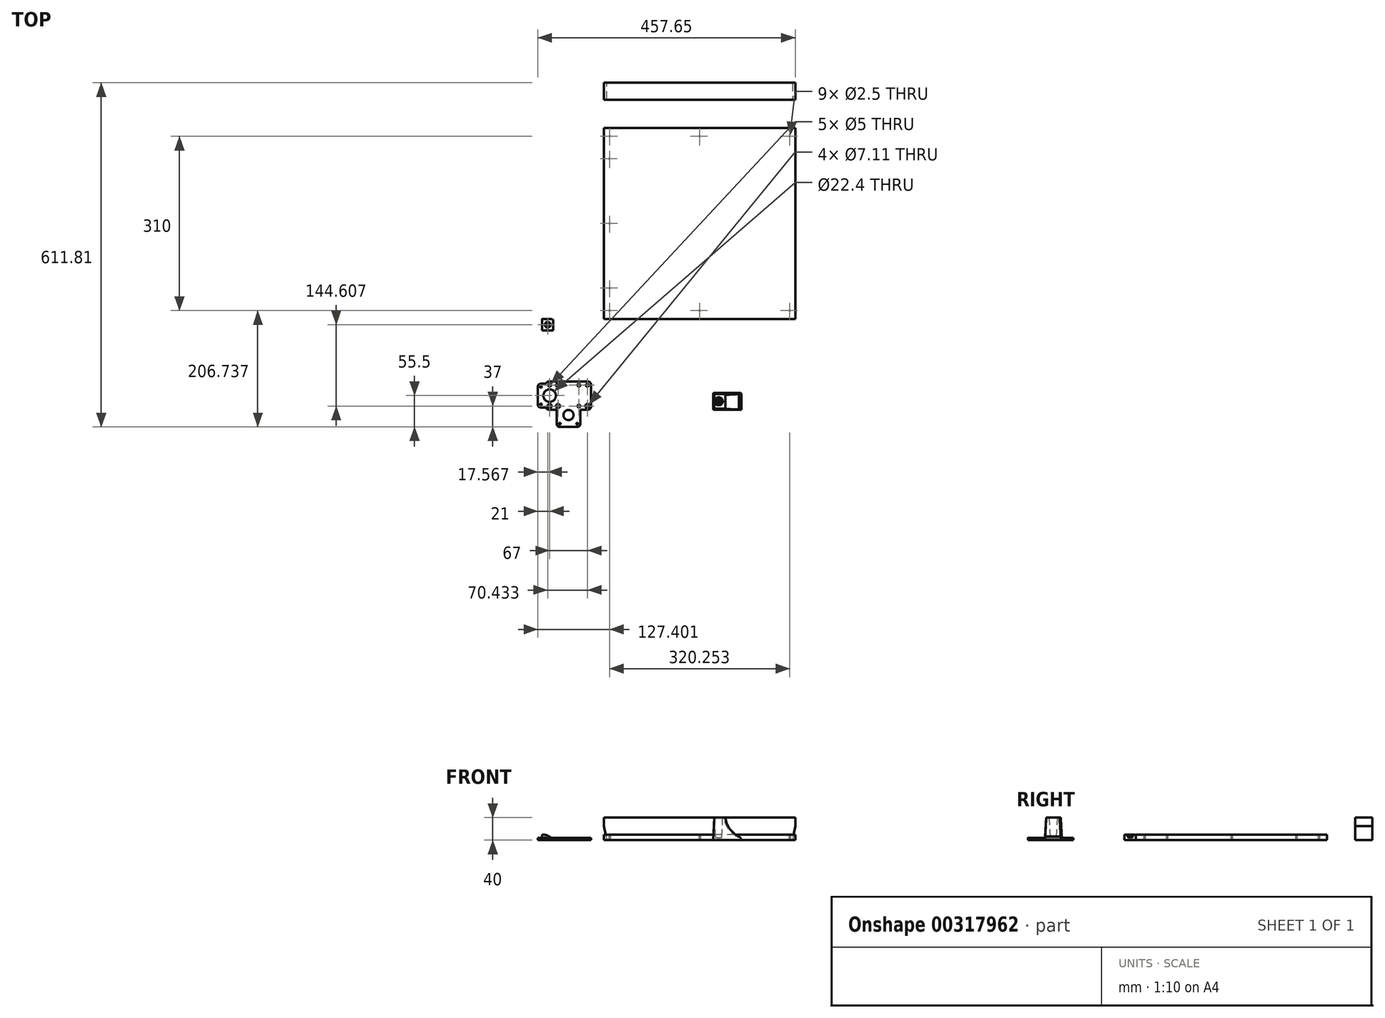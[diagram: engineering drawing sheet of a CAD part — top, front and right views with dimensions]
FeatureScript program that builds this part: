
annotation { "Feature Type Name" : "Feature", "Feature Type Description" : "" }
export const myFeature = defineFeature(function(context is Context, id is Id, definition is map)
    precondition{}
    {
        {
            var Q0;
            Q0=qCreatedBy(makeId("Top.planeOp"),FACE);
            var sketch = newSketch(context, id + "F0", { "sketchPlane" : qUnion([Q0])});
            skLineSegment(sketch, "E0.left", {"start": v(-18.5, 18.5) * mm, "end": v(-18.5, -18.5) * mm, "construction": true});
            skLineSegment(sketch, "E0.right", {"start": v(18.5, 18.5) * mm, "end": v(18.5, -18.5) * mm, "construction": true});
            skCircle(sketch, "E1", {"center": v(-18.5, 18.5) * mm, "radius": 3.56 * mm});
            skCircle(sketch, "E2", {"center": v(18.5, 18.5) * mm, "radius": 2.5 * mm});
            skCircle(sketch, "E3", {"center": v(18.5, -18.5) * mm, "radius": 2.5 * mm});
            skCircle(sketch, "E4", {"center": v(-18.5, -18.5) * mm, "radius": 3.56 * mm});
            skLineSegment(sketch, "E5.bottom", {"start": v(-35, 25) * mm, "end": v(35, 25) * mm});
            skLineSegment(sketch, "E5.top", {"start": v(-35, -25) * mm, "end": v(0.1, -25) * mm});
            skLineSegment(sketch, "E5.right", {"start": v(40, 20) * mm, "end": v(40, -20) * mm});
            skPoint(sketch, "E6.visualSharp", {"position": v(-40, 25) * mm});
            skArc(sketch, "E6.filletArc", {"start": v(-35, 25) * mm, "mid": v(-38.54, 23.54) * mm, "end": v(-40, 20) * mm});
            skPoint(sketch, "E7.visualSharp", {"position": v(40, 25) * mm});
            skArc(sketch, "E7.filletArc", {"start": v(40, 20) * mm, "mid": v(38.54, 23.54) * mm, "end": v(35, 25) * mm});
            skPoint(sketch, "E8.visualSharp", {"position": v(40, -25) * mm});
            skArc(sketch, "E8.filletArc", {"start": v(35, -25) * mm, "mid": v(38.54, -23.54) * mm, "end": v(40, -20) * mm});
            skPoint(sketch, "E9.visualSharp", {"position": v(-40, -25) * mm});
            skArc(sketch, "E9.filletArc", {"start": v(-40, -20) * mm, "mid": v(-38.54, -23.54) * mm, "end": v(-35, -25) * mm});
            skLineSegment(sketch, "E10.bottom", {"start": v(403.15, 136.24) * mm, "end": v(63.15, 136.24) * mm});
            skLineSegment(sketch, "E10.top", {"start": v(403.15, 476.24) * mm, "end": v(63.15, 476.24) * mm});
            skLineSegment(sketch, "E10.left", {"start": v(403.15, 136.24) * mm, "end": v(403.15, 476.24) * mm});
            skLineSegment(sketch, "E10.right", {"start": v(63.15, 136.24) * mm, "end": v(63.15, 476.24) * mm});
            skCircle(sketch, "E11", {"center": v(-33.5, -18.5) * mm, "radius": 3.56 * mm});
            skCircle(sketch, "E12", {"center": v(33.5, -18.5) * mm, "radius": 3.56 * mm});
            skCircle(sketch, "E13", {"center": v(-33.5, 18.5) * mm, "radius": 2.5 * mm});
            skCircle(sketch, "E14", {"center": v(33.5, 18.5) * mm, "radius": 2.5 * mm});
            skPoint(sketch, "E15.middle.positionSnap0", {"position": v(-40, 0) * mm});
            skPoint(sketch, "E15.centerSnap0", {"position": v(-40, 0) * mm});
            skLineSegment(sketch, "E16.top", {"start": v(-15.5, -50) * mm, "end": v(15.5, -50) * mm, "construction": true});
            skLineSegment(sketch, "E16.left", {"start": v(-15.5, -19) * mm, "end": v(-15.5, -50) * mm, "construction": true});
            skLineSegment(sketch, "E16.right", {"start": v(15.5, -19) * mm, "end": v(15.5, -50) * mm, "construction": true});
            skPoint(sketch, "E16.middle", {"position": v(0, -34.5) * mm});
            skLineSegment(sketch, "E17.bottom", {"start": v(21, -13.5) * mm, "end": v(18.5, -13.5) * mm});
            skLineSegment(sketch, "E17.top", {"start": v(16, -55.5) * mm, "end": v(-16, -55.5) * mm});
            skLineSegment(sketch, "E17.left", {"start": v(21, -25) * mm, "end": v(21, -50.5) * mm});
            skLineSegment(sketch, "E17.right", {"start": v(-21, -15.97) * mm, "end": v(-21, -21.03) * mm});
            skCircle(sketch, "E18", {"center": v(0, -34.5) * mm, "radius": 9 * mm});
            skCircle(sketch, "E19", {"center": v(-15.5, -50) * mm, "radius": 1.5 * mm});
            skCircle(sketch, "E20", {"center": v(15.5, -50) * mm, "radius": 1.5 * mm});
            skPoint(sketch, "E21.visualSharp", {"position": v(-21, -55.5) * mm});
            skArc(sketch, "E21.filletArc", {"start": v(-21, -50.5) * mm, "mid": v(-19.54, -54.04) * mm, "end": v(-16, -55.5) * mm});
            skPoint(sketch, "E22.visualSharp", {"position": v(21, -55.5) * mm});
            skArc(sketch, "E22.filletArc", {"start": v(16, -55.5) * mm, "mid": v(19.54, -54.04) * mm, "end": v(21, -50.5) * mm});
            skLineSegment(sketch, "E23.bottom", {"start": v(-49, 15.5) * mm, "end": v(-47.5, 15.5) * mm, "construction": true});
            skLineSegment(sketch, "E23.top", {"start": v(-49, -15.5) * mm, "end": v(-18, -15.5) * mm, "construction": true});
            skLineSegment(sketch, "E23.left", {"start": v(-49, 15.5) * mm, "end": v(-49, -15.5) * mm, "construction": true});
            skLineSegment(sketch, "E23.right", {"start": v(-18, 15.5) * mm, "end": v(-18, -15.5) * mm, "construction": true});
            skCircle(sketch, "E24", {"center": v(-33.5, 0) * mm, "radius": 11.2 * mm});
            skCircle(sketch, "E25", {"center": v(-49, -15.5) * mm, "radius": 1.5 * mm});
            skCircle(sketch, "E26", {"center": v(-49, 15.5) * mm, "radius": 1.5 * mm});
            skPoint(sketch, "E27.visualSharp", {"position": v(-13.5, -20) * mm});
            skLineSegment(sketch, "E28.trimOffspring", {"start": v(-40, 15.5) * mm, "end": v(-18, 15.5) * mm, "construction": true});
            skLineSegment(sketch, "E29.trimOffspring", {"start": v(-21, -25) * mm, "end": v(-21, -50.5) * mm});
            skLineSegment(sketch, "E30.trimOffspring", {"start": v(15.5, -25) * mm, "end": v(35, -25) * mm});
            skLineSegment(sketch, "E31.bottom", {"start": v(-49.5, 21) * mm, "end": v(-39.9, 21) * mm});
            skLineSegment(sketch, "E31.top", {"start": v(-49.5, -21) * mm, "end": v(-39.9, -21) * mm});
            skLineSegment(sketch, "E31.left", {"start": v(-54.5, 16) * mm, "end": v(-54.5, -16) * mm});
            skLineSegment(sketch, "E31.right", {"start": v(-12.5, 21) * mm, "end": v(-12.5, 18.5) * mm});
            skLineSegment(sketch, "E32.trimOffspring", {"start": v(-12.5, -13.5) * mm, "end": v(-12.5, -21) * mm});
            skPoint(sketch, "E33.visualSharp", {"position": v(-54.5, -21) * mm});
            skArc(sketch, "E33.filletArc", {"start": v(-54.5, -16) * mm, "mid": v(-53.04, -19.54) * mm, "end": v(-49.5, -21) * mm});
            skPoint(sketch, "E34.visualSharp", {"position": v(-54.5, 21) * mm});
            skArc(sketch, "E34.filletArc", {"start": v(-49.5, 21) * mm, "mid": v(-53.04, 19.54) * mm, "end": v(-54.5, 16) * mm});
            skLineSegment(sketch, "E35.right", {"start": v(257.17, 4.9) * mm, "end": v(257.17, -25.1) * mm});
            skCircle(sketch, "E36", {"center": v(267.17, -10.1) * mm, "radius": 5 * mm});
            skCircle(sketch, "E37", {"center": v(267.17, -10.1) * mm, "radius": 2 * mm});
            skLineSegment(sketch, "E38.right", {"start": v(307.17, -25.1) * mm, "end": v(307.17, 4.9) * mm});
            skLineSegment(sketch, "E39.bottom", {"start": v(-46.93, 136.1) * mm, "end": v(-26.93, 136.1) * mm});
            skLineSegment(sketch, "E39.top", {"start": v(-46.93, 116.1) * mm, "end": v(-26.93, 116.1) * mm});
            skLineSegment(sketch, "E39.left", {"start": v(-46.93, 136.1) * mm, "end": v(-46.93, 116.1) * mm});
            skLineSegment(sketch, "E39.right", {"start": v(-26.93, 136.1) * mm, "end": v(-26.93, 116.1) * mm});
            skCircle(sketch, "E40", {"center": v(-36.93, 126.1) * mm, "radius": 2.5 * mm});
            skPoint(sketch, "E40.centerSnap0", {"position": v(-36.93, 136.1) * mm});
            skPoint(sketch, "E40.centerSnap1", {"position": v(-46.93, 126.1) * mm});
            skCircle(sketch, "E41", {"center": v(-36.93, 126.1) * mm, "radius": 5 * mm});
            skLineSegment(sketch, "E42", {"start": v(73.15, 136.24) * mm, "end": v(73.15, 476.24) * mm, "construction": true});
            skPoint(sketch, "E43", {"position": v(73.15, 151.24) * mm});
            skPoint(sketch, "E44", {"position": v(73.15, 191.24) * mm});
            skPoint(sketch, "E45", {"position": v(73.15, 306.24) * mm});
            skPoint(sketch, "E46", {"position": v(73.15, 461.24) * mm});
            skPoint(sketch, "E47", {"position": v(72.9, 421.24) * mm});
            skLineSegment(sketch, "E48", {"start": v(257.17, -25.1) * mm, "end": v(307.17, -25.1) * mm});
            skLineSegment(sketch, "E49", {"start": v(307.17, 4.9) * mm, "end": v(257.17, 4.9) * mm});
            skLineSegment(sketch, "E50", {"start": v(393.15, 136.24) * mm, "end": v(393.15, 476.24) * mm, "construction": true});
            skPoint(sketch, "E51", {"position": v(393.15, 151.24) * mm});
            skPoint(sketch, "E52", {"position": v(393.15, 461.24) * mm});
            skLineSegment(sketch, "E53.bottom", {"start": v(63.15, 526.3) * mm, "end": v(403.15, 526.3) * mm});
            skLineSegment(sketch, "E53.top", {"start": v(63.15, 556.3) * mm, "end": v(403.15, 556.3) * mm});
            skLineSegment(sketch, "E53.left", {"start": v(63.15, 526.3) * mm, "end": v(63.15, 556.3) * mm});
            skLineSegment(sketch, "E53.right", {"start": v(403.15, 526.3) * mm, "end": v(403.15, 556.3) * mm});
            skLineSegment(sketch, "E54", {"start": v(73.15, 151.24) * mm, "end": v(393.15, 151.24) * mm, "construction": true});
            skLineSegment(sketch, "E55", {"start": v(73.15, 461.24) * mm, "end": v(393.15, 461.24) * mm, "construction": true});
            skPoint(sketch, "E56", {"position": v(233.15, 461.24) * mm});
            skPoint(sketch, "E57", {"position": v(233.15, 151.24) * mm});
            skSolve(sketch);
        }
        {
            var Q0;
            Q0=makeQuery(id+"F0.imprint","IMPRINT",FACE,{"disambiguationData":[TD([[makeQuery(id+"F0.imprint","IMPRINT",EDGE,{"derivedFrom":sQuery(id+"F0.wireOp",EDGE,"E1")}),-1.0]])]});
            var Q1;
            Q1=makeQuery(id+"F0.imprint","IMPRINT",FACE,{"disambiguationData":[TD([[makeQuery(id+"F0.imprint","IMPRINT",EDGE,{"derivedFrom":sQuery(id+"F0.wireOp",EDGE,"5QKgwCEY-hStk-wvY1-uHoH-thM2InlFBlLN.top")}),-1.0]])]});
            var Q2;
            Q2=makeQuery(id+"F0.imprint","IMPRINT",FACE,{"disambiguationData":[TD([[makeQuery(id+"F0.imprint","IMPRINT",EDGE,{"derivedFrom":sQuery(id+"F0.wireOp",EDGE,"DSqGHO2r-ZKHx-pAYN-DuYB-4O4wjz5FZ1oX.bottom")}),-1.0]])]});
            var Q3;
            Q3=makeQuery(id+"F0.imprint","IMPRINT",FACE,{"disambiguationData":[TD([[makeQuery(id+"F0.imprint","IMPRINT",EDGE,{"derivedFrom":sQuery(id+"F0.wireOp",EDGE,"HSy17Wos-LkgW-PUzs-iLZR-7mMcprWT0IVK.bottom")}),1.0]])]});
            var Q4;
            Q4=makeQuery(id+"F0.imprint","IMPRINT",FACE,{"disambiguationData":[TD([[makeQuery(id+"F0.imprint","IMPRINT",EDGE,{"derivedFrom":sQuery(id+"F0.wireOp",EDGE,"0c0f4aba-d832-4a81-b14c-29bbfecc0367.right")}),1.0]])]});
            extrude(context, id + "F1", {"entities" : qUnion([Q0, Q1, Q2, Q3, Q4]), "depth" : 4 * mm});
        }
        {
            var Q0;
            Q0=makeQuery(id+"F0.imprint","IMPRINT",FACE,{"disambiguationData":[TD([[makeQuery(id+"F0.imprint","IMPRINT",EDGE,{"derivedFrom":sQuery(id+"F0.wireOp",EDGE,"E10.bottom")}),-1.0]])]});
            extrude(context, id + "F2", {"entities" : qUnion([Q0]), "depth" : 10 * mm});
        }
        {
            var Q0;
            Q0=makeQuery(id+"F0.imprint","IMPRINT",FACE,{"disambiguationData":[TD([[makeQuery(id+"F0.imprint","IMPRINT",EDGE,{"derivedFrom":sQuery(id+"F0.wireOp",EDGE,"E35.bottom")}),1.0]])]});
            var Q1;
            Q1=makeQuery(id+"F0.imprint","IMPRINT",FACE,{"disambiguationData":[TD([[makeQuery(id+"F0.imprint","IMPRINT",EDGE,{"derivedFrom":sQuery(id+"F0.wireOp",EDGE,"E35.right")}),1.0]])]});
            extrude(context, id + "F3", {"entities" : qUnion([Q0, Q1]), "depth" : 40 * mm, "hasDraft" : true, "draftAngle" : 3 * degree, "draftPullDirection" : true});
        }
        {
            var Q0;
            Q0=makeQuery(id+"F0.imprint","IMPRINT",FACE,{"disambiguationData":[TD([[makeQuery(id+"F0.imprint","IMPRINT",EDGE,{"derivedFrom":sQuery(id+"F0.wireOp",EDGE,"E36")}),1.0]])]});
            extrude(context, id + "F4", {"entities" : qUnion([Q0]), "operationType" : NewBodyOperationType.ADD, "depth" : 4 * mm, "hasDraft" : true, "draftAngle" : 3 * degree});
        }
        {
            var Q0;
            Q0=qCreatedBy(makeId("Front.planeOp"),FACE);
            var sketch = newSketch(context, id + "F5", { "sketchPlane" : qUnion([Q0])});
            skArc(sketch, "E58", {"start": v(307.17, 0) * mm, "mid": v(305.91, 3.8) * mm, "end": v(302.9, 6.41) * mm});
            skArc(sketch, "E59", {"start": v(278.53, 41.5) * mm, "mid": v(286.23, 20.84) * mm, "end": v(302.9, 6.41) * mm});
            skLineSegment(sketch, "E60", {"start": v(278.53, 41.5) * mm, "end": v(307.17, 41.5) * mm});
            skLineSegment(sketch, "E61", {"start": v(307.17, 41.5) * mm, "end": v(307.17, 0) * mm});
            skSolve(sketch);
        }
        {
            var Q0;
            {var subQ0=sQuery(id+"F5.wireOp",EDGE,"E58");Q0=makeQuery(id+"F5.imprint","IMPRINT",FACE,{"disambiguationData":[TD([[makeQuery(id+"F5.imprint","IMPRINT",EDGE,{"derivedFrom":subQ0}),-1.0]])]});}
            var Q1;
            {var subQ0=sQuery(id+"F5.wireOp",EDGE,"E60");Q1=makeQuery(id+"F5.imprint","IMPRINT",FACE,{"disambiguationData":[TD([[makeQuery(id+"F5.imprint","IMPRINT",EDGE,{"derivedFrom":subQ0}),-1.0]])]});}
            extrude(context, id + "F6", {"entities" : qUnion([Q0, Q1]), "operationType" : NewBodyOperationType.REMOVE, "depth" : 39.1 * mm, "hasSecondDirection" : true, "secondDirectionOppositeDirection" : true, "secondDirectionDepth" : 25 * mm});
        }
        {
            var Q0;
            Q0=makeQuery(id+"F3.opExtrude","SWEPT_EDGE",EDGE,{"disambiguationData":[OSD([sQuery(id+"F0.wireOp",EDGE,"E35.right"),sQuery(id+"F0.wireOp",EDGE,"E49")])]});
            var Q1;
            Q1=makeQuery(id+"F3.opExtrude","SWEPT_EDGE",EDGE,{"disambiguationData":[OSD([sQuery(id+"F0.wireOp",EDGE,"E35.right"),sQuery(id+"F0.wireOp",EDGE,"E48")])]});
            var Q2;
            Q2=makeQuery(id+"F3.opExtrude","SWEPT_EDGE",EDGE,{"disambiguationData":[OSD([sQuery(id+"F0.wireOp",EDGE,"E35.right"),sQuery(id+"F0.wireOp",EDGE,"E49")])]});
            var Q3;
            Q3=makeQuery(id+"F6.boolean.opBoolean","COPY",EDGE,{"derivedFrom":makeQuery(id+"F6.opExtrude","CAP_EDGE",EDGE,{"disambiguationData":[OSD([sQuery(id+"F5.wireOp",EDGE,"E58")])],"isStart":true})});
            var Q4;
            {var subQ0=sQuery(id+"F0.wireOp",EDGE,"E36");Q4=makeQuery(id+"F6.boolean.opBoolean","INTERSECT",EDGE,{"derivedFrom":[makeQuery(id+"F4.boolean.opBoolean","MERGE",FACE,{"derivedFrom":[makeQuery(id+"F3.opExtrude","CAP_FACE",FACE,{"disambiguationData":[OSD([sQuery(id+"F0.wireOp",EDGE,"E35.right"),subQ0,sQuery(id+"F0.wireOp",EDGE,"E38.right"),sQuery(id+"F0.wireOp",EDGE,"E48"),sQuery(id+"F0.wireOp",EDGE,"E49")])],"isStart":true}),makeQuery(id+"F4.opExtrude","CAP_FACE",FACE,{"disambiguationData":[OSD([subQ0,sQuery(id+"F0.wireOp",EDGE,"E37")])],"isStart":true})]}),makeQuery(id+"F6.opExtrude","SWEPT_FACE",FACE,{"disambiguationData":[OSD([sQuery(id+"F5.wireOp",EDGE,"E58")])]})]});}
            var Q5;
            Q5=makeQuery(id+"F6.boolean.opBoolean","INTERSECT",EDGE,{"derivedFrom":[makeQuery(id+"F3.opExtrude","SWEPT_FACE",FACE,{"disambiguationData":[OSD([sQuery(id+"F0.wireOp",EDGE,"E49")])]}),makeQuery(id+"F6.opExtrude","SWEPT_FACE",FACE,{"disambiguationData":[OSD([sQuery(id+"F5.wireOp",EDGE,"E58")])]})]});
            fillet(context, id + "F7", {"entities" : qUnion([Q0, Q1, Q2, Q3, Q4, Q5]), "radius" : 2 * mm, "tangentPropagation" : true, "allowEdgeOverflow" : false});
        }
        {
            var Q0;
            Q0=makeQuery(id+"F0.imprint","IMPRINT",FACE,{"disambiguationData":[TD([[makeQuery(id+"F0.imprint","IMPRINT",EDGE,{"derivedFrom":sQuery(id+"F0.wireOp",EDGE,"E39.bottom")}),-1.0]])]});
            extrude(context, id + "F8", {"entities" : qUnion([Q0]), "depth" : 10 * mm});
        }
        {
            var Q0;
            Q0=makeQuery(id+"F0.imprint","IMPRINT",FACE,{"disambiguationData":[TD([[makeQuery(id+"F0.imprint","IMPRINT",EDGE,{"derivedFrom":sQuery(id+"F0.wireOp",EDGE,"E40")}),-1.0]])]});
            extrude(context, id + "F9", {"entities" : qUnion([Q0]), "operationType" : NewBodyOperationType.ADD, "depth" : 4 * mm});
        }
        {
            var Q0;
            Q0=makeQuery(id+"F8.opExtrude","SWEPT_FACE",FACE,{"disambiguationData":[OSD([sQuery(id+"F0.wireOp",EDGE,"E39.top")])]});
            var sketch = newSketch(context, id + "F10", { "sketchPlane" : qUnion([Q0])});
            skArc(sketch, "E62", {"start": v(-26.93, 0) * mm, "mid": v(-35.75, 7.36) * mm, "end": v(-46.93, 10) * mm});
            skSolve(sketch);
        }
        {
            var Q0;
            Q0=makeQuery(id+"F10.imprint","IMPRINT",FACE,{"disambiguationData":[TD([[makeQuery(id+"F10.imprint","IMPRINT",EDGE,{"derivedFrom":sQuery(id+"F10.wireOp",EDGE,"E62")}),-1.0]])]});
            extrude(context, id + "F11", {"entities" : qUnion([Q0]), "operationType" : NewBodyOperationType.REMOVE, "oppositeDirection" : true, "depth" : 25 * mm});
        }
        {
            var Q0;
            Q0=makeQuery(id+"F11.boolean.opBoolean","COPY",EDGE,{"derivedFrom":makeQuery(id+"F11.opExtrude","CAP_EDGE",EDGE,{"disambiguationData":[OSD([sQuery(id+"F10.wireOp",EDGE,"E62")])],"isStart":true})});
            var Q1;
            Q1=makeQuery(id+"F11.boolean.opBoolean","INTERSECT",EDGE,{"derivedFrom":[makeQuery(id+"F8.opExtrude","SWEPT_FACE",FACE,{"disambiguationData":[OSD([sQuery(id+"F0.wireOp",EDGE,"E39.bottom")])]}),makeQuery(id+"F11.opExtrude","SWEPT_FACE",FACE,{"disambiguationData":[OSD([sQuery(id+"F10.wireOp",EDGE,"E62")])]})]});
            fillet(context, id + "F12", {"entities" : qUnion([Q0, Q1]), "radius" : 3 * mm, "tangentPropagation" : true, "allowEdgeOverflow" : false});
        }
        {
            var Q0;
            Q0=sQuery(id+"F0.wireOp",VERTEX,"E43");
            var Q1;
            Q1=sQuery(id+"F0.wireOp",VERTEX,"E44");
            var Q2;
            Q2=sQuery(id+"F0.wireOp",VERTEX,"E45");
            var Q3;
            Q3=sQuery(id+"F0.wireOp",VERTEX,"E47");
            var Q4;
            Q4=sQuery(id+"F0.wireOp",VERTEX,"E46");
            var Q5;
            Q5=sQuery(id+"F0.wireOp",VERTEX,"E51");
            var Q6;
            Q6=sQuery(id+"F0.wireOp",VERTEX,"E52");
            var Q7;
            Q7=sQuery(id+"F0.wireOp",VERTEX,"E56");
            var Q8;
            Q8=sQuery(id+"F0.wireOp",VERTEX,"E57");
            var Q9;
            Q9=makeQuery(id+"F2.opExtrude","SWEPT_BODY",BODY,{"disambiguationData":[OSD([sQuery(id+"F0.wireOp",EDGE,"E10.bottom"),sQuery(id+"F0.wireOp",EDGE,"E10.top"),sQuery(id+"F0.wireOp",EDGE,"E10.left"),sQuery(id+"F0.wireOp",EDGE,"E10.right")])]});
            hole(context, id + "F13", {"style" : HoleStyle.SIMPLE, "endStyle" : HoleEndStyle.BLIND, "oppositeDirection" : true, "holeDiameter" : 2.5 * mm, "holeDepth" : 8 * mm, "tappedDepth" : 12 * mm, "tapClearance" : 3, "locations" : qUnion([Q0, Q1, Q2, Q3, Q4, Q5, Q6, Q7, Q8]), "scope" : qUnion([Q9])});
        }
        {
            var Q0;
            Q0=makeQuery(id+"F0.imprint","IMPRINT",FACE,{"disambiguationData":[TD([[makeQuery(id+"F0.imprint","IMPRINT",EDGE,{"derivedFrom":sQuery(id+"F0.wireOp",EDGE,"E53.bottom")}),1.0]])]});
            extrude(context, id + "F14", {"entities" : qUnion([Q0]), "depth" : 40 * mm});
        }
        {
            var Q0;
            Q0=makeQuery(id+"F14.opExtrude","CAP_EDGE",EDGE,{"disambiguationData":[OSD([sQuery(id+"F0.wireOp",EDGE,"E53.left")])],"isStart":true});
            var Q1;
            Q1=makeQuery(id+"F14.opExtrude","CAP_EDGE",EDGE,{"disambiguationData":[OSD([sQuery(id+"F0.wireOp",EDGE,"E53.right")])],"isStart":true});
            chamfer(context, id + "F15", {"entities" : qUnion([Q0, Q1]), "chamferType" : ChamferType.TWO_OFFSETS, "width1" : 5 * mm, "oppositeDirection" : false, "width2" : 25 * mm, "tangentPropagation" : true});
        }
    });
